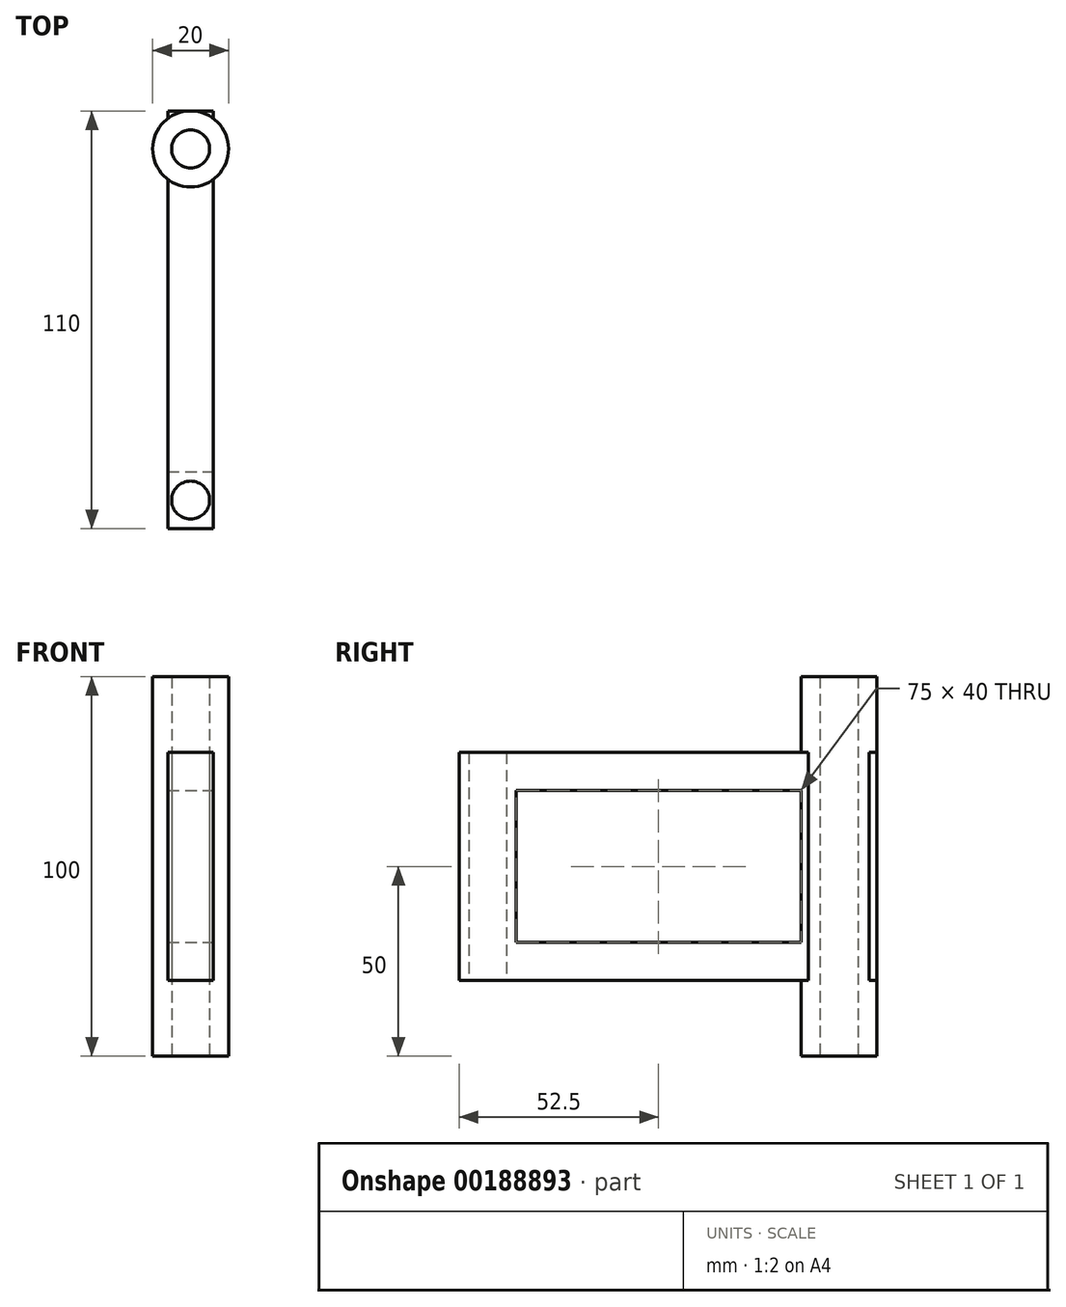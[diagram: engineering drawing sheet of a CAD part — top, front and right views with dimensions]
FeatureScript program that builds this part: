
annotation { "Feature Type Name" : "Feature", "Feature Type Description" : "" }
export const myFeature = defineFeature(function(context is Context, id is Id, definition is map)
    precondition{}
    {
        {
            var Q0;
            Q0=qCreatedBy(makeId("Top.planeOp"),FACE);
            var sketch = newSketch(context, id + "F0", { "sketchPlane" : qUnion([Q0])});
            skCircle(sketch, "E0", {"center": v(0, 0) * mm, "radius": 10 * mm});
            skSolve(sketch);
        }
        {
            var Q0;
            Q0=qSketchRegion(id+"F0",true);
            extrude(context, id + "F1", {"entities" : qUnion([Q0]), "depth" : 100 * mm});
        }
        {
            var Q0;
            Q0=qCreatedBy(makeId("Front.planeOp"),FACE);
            var sketch = newSketch(context, id + "F2", { "sketchPlane" : qUnion([Q0])});
            skLineSegment(sketch, "E1.bottom", {"start": v(6, 20) * mm, "end": v(-6, 20) * mm});
            skLineSegment(sketch, "E1.top", {"start": v(6, 80) * mm, "end": v(-6, 80) * mm});
            skLineSegment(sketch, "E1.left", {"start": v(6, 20) * mm, "end": v(6, 80) * mm});
            skLineSegment(sketch, "E1.right", {"start": v(-6, 20) * mm, "end": v(-6, 80) * mm});
            skPoint(sketch, "E1.middle", {"position": v(0, 50) * mm});
            skSolve(sketch);
        }
        {
            var Q0;
            Q0=qSketchRegion(id+"F2",true);
            extrude(context, id + "F3", {"entities" : qUnion([Q0]), "operationType" : NewBodyOperationType.ADD, "depth" : 100 * mm, "hasSecondDirection" : true, "secondDirectionOppositeDirection" : true, "secondDirectionDepth" : 10 * mm});
        }
        {
            var Q0;
            Q0=makeQuery(id+"F3.opExtrude","SWEPT_FACE",FACE,{"disambiguationData":[OSD([sQuery(id+"F2.wireOp",EDGE,"E1.left")])]});
            var sketch = newSketch(context, id + "F4", { "sketchPlane" : qUnion([Q0])});
            skLineSegment(sketch, "E2.bottom", {"start": v(-10, 30) * mm, "end": v(-85, 30) * mm});
            skLineSegment(sketch, "E2.top", {"start": v(-10, 70) * mm, "end": v(-85, 70) * mm});
            skLineSegment(sketch, "E2.left", {"start": v(-10, 30) * mm, "end": v(-10, 70) * mm});
            skLineSegment(sketch, "E2.right", {"start": v(-85, 30) * mm, "end": v(-85, 70) * mm});
            skSolve(sketch);
        }
        {
            var Q0;
            Q0=qSketchRegion(id+"F4",true);
            extrude(context, id + "F5", {"entities" : qUnion([Q0]), "operationType" : NewBodyOperationType.REMOVE, "endBound" : BoundingType.UP_TO_NEXT, "oppositeDirection" : true, "depth" : 25 * mm});
        }
        {
            var Q0;
            Q0=qCreatedBy(makeId("Top.planeOp"),FACE);
            var sketch = newSketch(context, id + "F6", { "sketchPlane" : qUnion([Q0])});
            skCircle(sketch, "E3", {"center": v(0, 0) * mm, "radius": 5 * mm});
            skSolve(sketch);
        }
        {
            var Q0;
            Q0=qSketchRegion(id+"F6",true);
            extrude(context, id + "F7", {"entities" : qUnion([Q0]), "operationType" : NewBodyOperationType.REMOVE, "endBound" : BoundingType.UP_TO_NEXT, "depth" : 25 * mm});
        }
        {
            var Q0;
            {var subQ0=sQuery(id+"F2.wireOp",EDGE,"E1.left");var subQ1=sQuery(id+"F2.wireOp",EDGE,"E1.right");var subQ2=sQuery(id+"F2.wireOp",EDGE,"E1.bottom");var subQ3=makeQuery(id+"F3.opExtrude","SWEPT_FACE",FACE,{"disambiguationData":[OSD([subQ2])]});Q0=makeQuery(id+"F3.boolean.opBoolean","SPLIT",FACE,{"disambiguationData":[TD([makeQuery(id+"F1.opExtrude","SWEPT_FACE",FACE,{"disambiguationData":[OSD([sQuery(id+"F0.wireOp",EDGE,"E0")])]}),subQ3,makeQuery(id+"F3.opExtrude","CAP_FACE",FACE,{"disambiguationData":[OSD([subQ2,sQuery(id+"F2.wireOp",EDGE,"E1.top"),subQ0,subQ1])],"isStart":false}),makeQuery(id+"F3.opExtrude","SWEPT_FACE",FACE,{"disambiguationData":[OSD([subQ0])]}),makeQuery(id+"F3.opExtrude","SWEPT_FACE",FACE,{"disambiguationData":[OSD([subQ1])]})])],"derivedFrom":subQ3});}
            var sketch = newSketch(context, id + "F8", { "sketchPlane" : qUnion([Q0])});
            skCircle(sketch, "E4", {"center": v(0, 92.5) * mm, "radius": 5 * mm});
            skPoint(sketch, "E5", {"position": v(0, 10) * mm});
            skSolve(sketch);
        }
        {
            var Q0;
            Q0=qSketchRegion(id+"F8",true);
            extrude(context, id + "F9", {"entities" : qUnion([Q0]), "operationType" : NewBodyOperationType.REMOVE, "endBound" : BoundingType.THROUGH_ALL, "oppositeDirection" : true, "depth" : 25 * mm});
        }
    });
